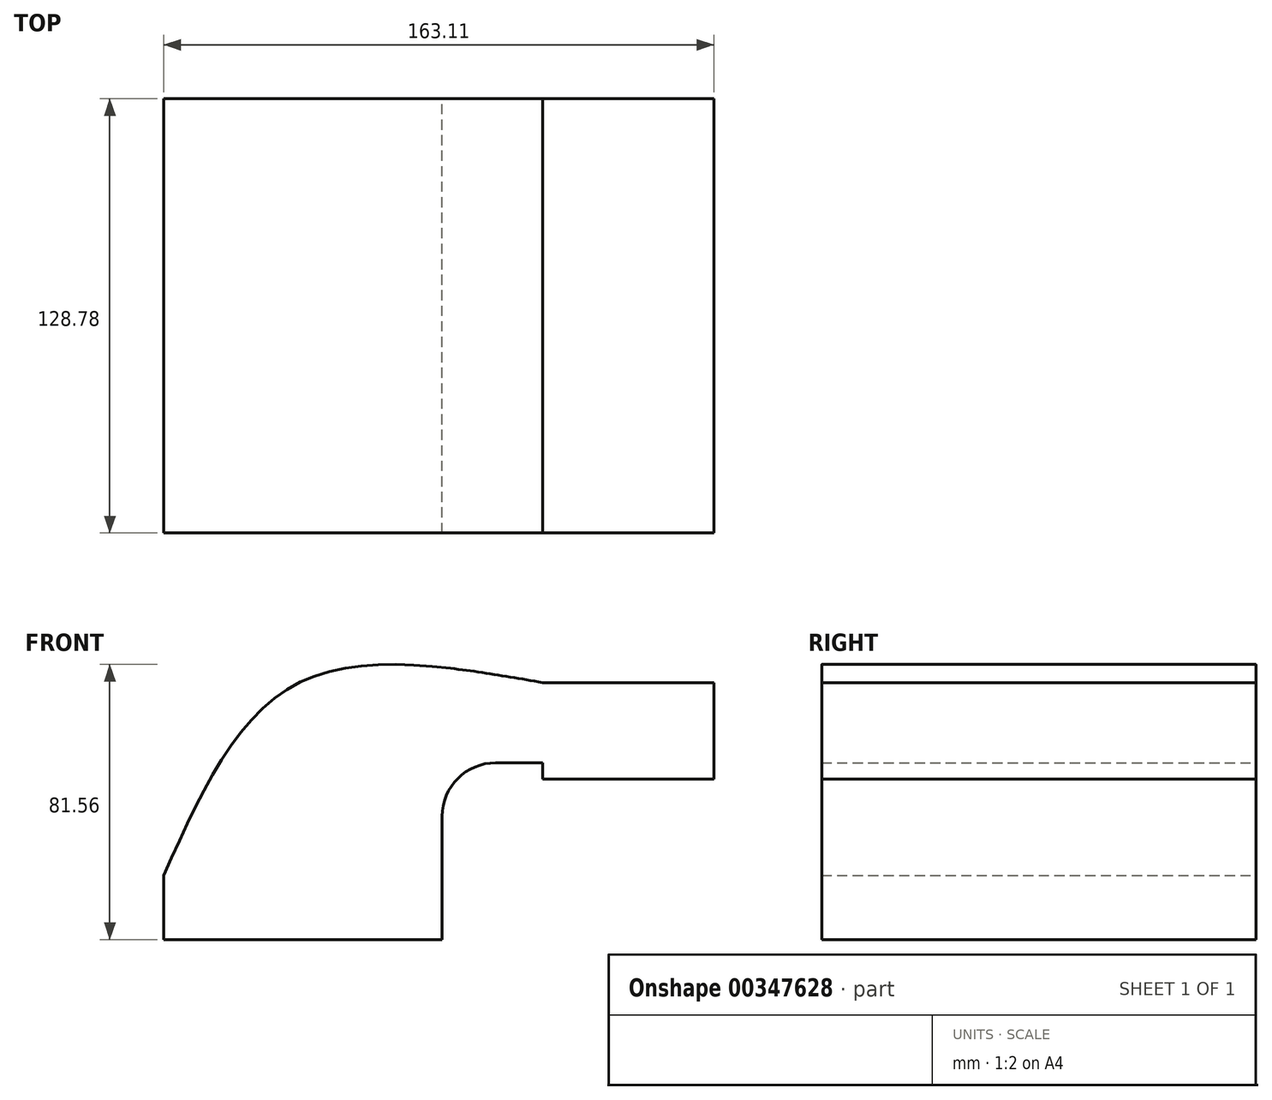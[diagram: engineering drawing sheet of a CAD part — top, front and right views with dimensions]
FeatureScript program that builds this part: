
annotation { "Feature Type Name" : "Feature", "Feature Type Description" : "" }
export const myFeature = defineFeature(function(context is Context, id is Id, definition is map)
    precondition{}
    {
        {
            var Q0;
            Q0=qCreatedBy(makeId("Front.planeOp"),FACE);
            var sketch = newSketch(context, id + "F0", { "sketchPlane" : qUnion([Q0])});
            skLineSegment(sketch, "E0.bottom", {"start": v(-41.28, 9.52) * mm, "end": v(41.28, 9.52) * mm});
            skLineSegment(sketch, "E0.top", {"start": v(-41.28, -9.53) * mm, "end": v(41.27, -9.53) * mm});
            skLineSegment(sketch, "E0.left", {"start": v(-41.28, 9.52) * mm, "end": v(-41.28, -9.53) * mm});
            skLineSegment(sketch, "E0.right", {"start": v(41.27, 9.52) * mm, "end": v(41.27, -9.53) * mm});
            skPoint(sketch, "E0.middle", {"position": v(0, 0) * mm});
            skLineSegment(sketch, "E1.bottom", {"start": v(71.03, 66.67) * mm, "end": v(121.83, 66.67) * mm});
            skLineSegment(sketch, "E1.top", {"start": v(71.03, 38.1) * mm, "end": v(121.83, 38.1) * mm});
            skLineSegment(sketch, "E1.left", {"start": v(71.03, 66.67) * mm, "end": v(71.03, 38.1) * mm});
            skLineSegment(sketch, "E1.right", {"start": v(121.83, 66.67) * mm, "end": v(121.83, 38.1) * mm});
            skLineSegment(sketch, "E2", {"start": v(41.27, 9.52) * mm, "end": v(41.27, 27) * mm});
            skArc(sketch, "E3", {"start": v(41.27, 27) * mm, "mid": v(45.92, 38.23) * mm, "end": v(57.15, 42.88) * mm});
            skLineSegment(sketch, "E4", {"start": v(57.15, 42.88) * mm, "end": v(96.43, 42.88) * mm});
            skLineSegment(sketch, "E5", {"start": v(96.43, 66.67) * mm, "end": v(96.43, 38.1) * mm});
            skLineSegment(sketch, "E6.0", {"start": v(57.15, 61.93) * mm, "end": v(96.43, 61.93) * mm});
            skArc(sketch, "E6.1", {"start": v(22.22, 27) * mm, "mid": v(32.45, 51.7) * mm, "end": v(57.15, 61.93) * mm});
            skLineSegment(sketch, "E6.2", {"start": v(22.22, 9.52) * mm, "end": v(22.22, 27) * mm});
            skFitSpline(sketch, "E7", {"points": [v(-41.28, 9.52) * mm, v(-2.07, 66.16) * mm, v(71.03, 66.67) * mm], "startDerivative": vector(63.7, 143.05) * mm, "endDerivative": vector(160.43, -27.9) * mm});
            skFitSpline(sketch, "E8", {"points": [v(43.9, 71.4) * mm, v(43.9, 66.67) * mm], "startDerivative": vector(0, -4.72) * mm, "endDerivative": vector(18.49, 16.96) * mm});
            skSolve(sketch);
        }
        {
            var Q0;
            {var subQ0=sQuery(id+"F0.wireOp",EDGE,"E6.1");Q0=makeQuery(id+"F0.imprint","IMPRINT",FACE,{"disambiguationData":[TD([[makeQuery(id+"F0.imprint","IMPRINT",EDGE,{"derivedFrom":subQ0}),1.0]])]});}
            extrude(context, id + "F1", {"entities" : qUnion([Q0]), "depth" : 25.4 * mm, "offsetDistance" : 25.4 * mm});
        }
        {
            var Q0;
            Q0 = qSketchRegion(id + "F0", true);
            extrude(context, id + "F2", {"entities" : qUnion([Q0]), "operationType" : NewBodyOperationType.ADD, "depth" : 128.78 * mm, "offsetDistance" : 25.4 * mm});
        }
    });
